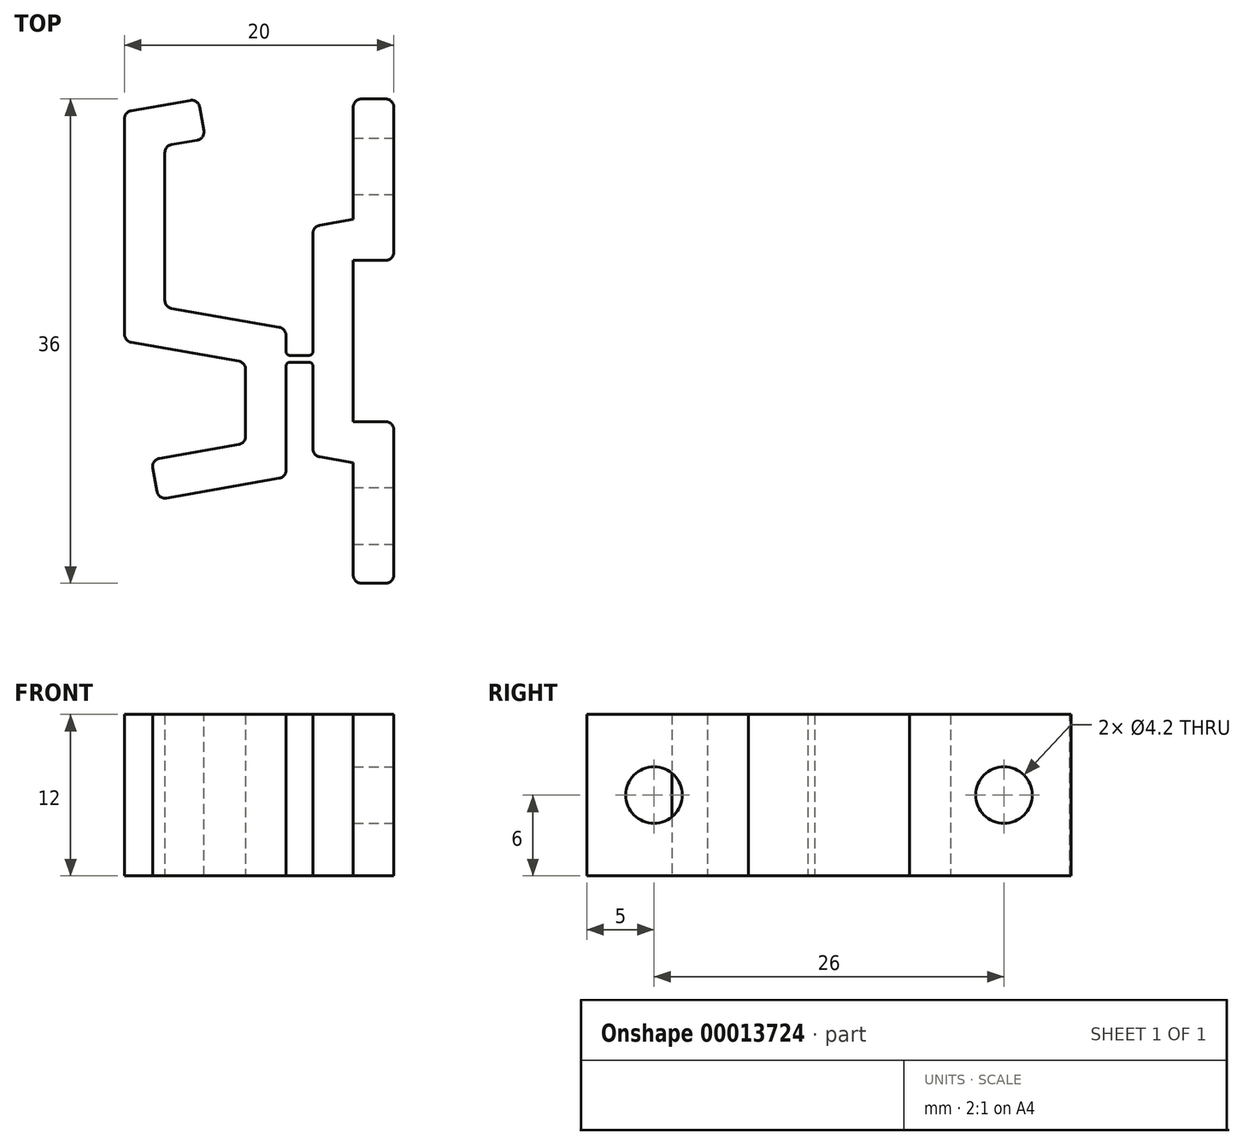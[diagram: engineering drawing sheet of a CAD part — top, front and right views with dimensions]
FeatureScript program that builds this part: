
annotation { "Feature Type Name" : "Feature", "Feature Type Description" : "" }
export const myFeature = defineFeature(function(context is Context, id is Id, definition is map)
    precondition{}
    {
        {
            var Q0;
            Q0=qCreatedBy(makeId("Top.planeOp"),FACE);
            var sketch = newSketch(context, id + "F0", { "sketchPlane" : qUnion([Q0])});
            skLineSegment(sketch, "E0", {"start": v(0, 0) * mm, "end": v(0, -12) * mm});
            skLineSegment(sketch, "E1", {"start": v(0, -12) * mm, "end": v(3, -12) * mm});
            skLineSegment(sketch, "E2", {"start": v(3, -12) * mm, "end": v(3, -24) * mm});
            skLineSegment(sketch, "E3", {"start": v(3, -24) * mm, "end": v(0, -24) * mm});
            skLineSegment(sketch, "E4", {"start": v(0, -24) * mm, "end": v(0, -15.05) * mm});
            skLineSegment(sketch, "E5", {"start": v(0, -15.05) * mm, "end": v(-3, -14.52) * mm});
            skLineSegment(sketch, "E6", {"start": v(-3, -14.52) * mm, "end": v(-3, 2.52) * mm});
            skLineSegment(sketch, "E7", {"start": v(-3, 2.52) * mm, "end": v(0, 3.05) * mm});
            skLineSegment(sketch, "E8", {"start": v(0, 3.05) * mm, "end": v(0, 12) * mm});
            skLineSegment(sketch, "E9", {"start": v(0, 12) * mm, "end": v(3, 12) * mm});
            skLineSegment(sketch, "E10", {"start": v(3, 12) * mm, "end": v(3, 0) * mm});
            skLineSegment(sketch, "E11", {"start": v(0, 0) * mm, "end": v(3, 0) * mm});
            skLineSegment(sketch, "E12", {"start": v(-5, -5.07) * mm, "end": v(-5, -16.1) * mm});
            skLineSegment(sketch, "E13", {"start": v(-5, -5.07) * mm, "end": v(-14, -3.48) * mm});
            skLineSegment(sketch, "E14", {"start": v(-5, -16.1) * mm, "end": v(-14.48, -17.78) * mm});
            skLineSegment(sketch, "E15", {"start": v(-14.48, -17.78) * mm, "end": v(-15, -14.82) * mm});
            skLineSegment(sketch, "E16", {"start": v(-15, -14.82) * mm, "end": v(-8, -13.59) * mm});
            skLineSegment(sketch, "E17", {"start": v(-8, -13.59) * mm, "end": v(-8, -7.59) * mm});
            skLineSegment(sketch, "E18", {"start": v(-8, -7.59) * mm, "end": v(-17, -6) * mm});
            skLineSegment(sketch, "E19", {"start": v(-14, -3.48) * mm, "end": v(-14, 8.52) * mm});
            skLineSegment(sketch, "E20", {"start": v(-14, 8.52) * mm, "end": v(-11, 9.05) * mm});
            skLineSegment(sketch, "E21", {"start": v(-11.52, 12) * mm, "end": v(-17, 11.03) * mm});
            skLineSegment(sketch, "E22", {"start": v(-17, 11.03) * mm, "end": v(-17, -6) * mm});
            skLineSegment(sketch, "E23", {"start": v(-11.52, 12) * mm, "end": v(-11, 9.05) * mm});
            skLineSegment(sketch, "E24", {"start": v(-3, -7.57) * mm, "end": v(-5, -7.57) * mm});
            skLineSegment(sketch, "E25", {"start": v(-3, -7.07) * mm, "end": v(-5, -7.07) * mm});
            skSolve(sketch);
        }
        {
            var Q0;
            {var subQ1=sQuery(id+"F0.wireOp",EDGE,"E13");Q0=makeQuery(id+"F0.imprint","IMPRINT",FACE,{"disambiguationData":[TD([[makeQuery(id+"F0.imprint","IMPRINT",EDGE,{"derivedFrom":subQ1}),1.0]])]});}
            var Q1;
            {var subQ1=sQuery(id+"F0.wireOp",EDGE,"E24");Q1=makeQuery(id+"F0.imprint","IMPRINT",FACE,{"disambiguationData":[TD([[makeQuery(id+"F0.imprint","IMPRINT",EDGE,{"derivedFrom":subQ1}),-1.0]])]});}
            var Q2;
            Q2=makeQuery(id+"F0.imprint","IMPRINT",FACE,{"disambiguationData":[TD([[makeQuery(id+"F0.imprint","IMPRINT",EDGE,{"derivedFrom":sQuery(id+"F0.wireOp",EDGE,"E0")}),-1.0]])]});
            extrude(context, id + "F1", {"entities" : qUnion([Q0, Q1, Q2]), "depth" : 12 * mm});
        }
        {
            var Q0;
            Q0=makeQuery(id+"F1.opExtrude","SWEPT_FACE",FACE,{"disambiguationData":[OSD([sQuery(id+"F0.wireOp",EDGE,"E2")])]});
            var sketch = newSketch(context, id + "F2", { "sketchPlane" : qUnion([Q0])});
            skLineSegment(sketch, "E26", {"start": v(-24, 6) * mm, "end": v(-19, 6) * mm, "construction": true});
            skLineSegment(sketch, "E27.0", {"start": v(12, 12) * mm, "end": v(12, 0) * mm});
            skLineSegment(sketch, "E28", {"start": v(12, 6) * mm, "end": v(7, 6) * mm, "construction": true});
            skCircle(sketch, "E29", {"center": v(-19, 6) * mm, "radius": 2.1 * mm});
            skCircle(sketch, "E30", {"center": v(7, 6) * mm, "radius": 2.1 * mm});
            skSolve(sketch);
        }
        {
            var Q0;
            Q0=makeQuery(id+"F2.imprint","IMPRINT",FACE,{"disambiguationData":[TD([[makeQuery(id+"F2.imprint","IMPRINT",EDGE,{"derivedFrom":sQuery(id+"F2.wireOp",EDGE,"E29")}),1.0]])]});
            var Q1;
            Q1=makeQuery(id+"F2.imprint","IMPRINT",FACE,{"disambiguationData":[TD([[makeQuery(id+"F2.imprint","IMPRINT",EDGE,{"derivedFrom":sQuery(id+"F2.wireOp",EDGE,"E30")}),1.0]])]});
            extrude(context, id + "F3", {"entities" : qUnion([Q0, Q1]), "operationType" : NewBodyOperationType.REMOVE, "endBound" : BoundingType.UP_TO_NEXT, "oppositeDirection" : true, "depth" : 25 * mm});
        }
        {
            var Q0;
            Q0=makeQuery(id+"F1.opExtrude","SWEPT_EDGE",EDGE,{"disambiguationData":[OSD([sQuery(id+"F0.wireOp",EDGE,"E21"),sQuery(id+"F0.wireOp",EDGE,"E23")])]});
            var Q1;
            Q1=makeQuery(id+"F1.opExtrude","SWEPT_EDGE",EDGE,{"disambiguationData":[OSD([sQuery(id+"F0.wireOp",EDGE,"E21"),sQuery(id+"F0.wireOp",EDGE,"E22")])]});
            var Q2;
            Q2=makeQuery(id+"F1.opExtrude","SWEPT_EDGE",EDGE,{"disambiguationData":[OSD([sQuery(id+"F0.wireOp",EDGE,"E18"),sQuery(id+"F0.wireOp",EDGE,"E22")])]});
            var Q3;
            Q3=makeQuery(id+"F1.opExtrude","SWEPT_EDGE",EDGE,{"disambiguationData":[OSD([sQuery(id+"F0.wireOp",EDGE,"E17"),sQuery(id+"F0.wireOp",EDGE,"E18")])]});
            var Q4;
            Q4=makeQuery(id+"F1.opExtrude","SWEPT_EDGE",EDGE,{"disambiguationData":[OSD([sQuery(id+"F0.wireOp",EDGE,"E16"),sQuery(id+"F0.wireOp",EDGE,"E17")])]});
            var Q5;
            Q5=makeQuery(id+"F1.opExtrude","SWEPT_EDGE",EDGE,{"disambiguationData":[OSD([sQuery(id+"F0.wireOp",EDGE,"E15"),sQuery(id+"F0.wireOp",EDGE,"E16")])]});
            var Q6;
            Q6=makeQuery(id+"F1.opExtrude","SWEPT_EDGE",EDGE,{"disambiguationData":[OSD([sQuery(id+"F0.wireOp",EDGE,"E14"),sQuery(id+"F0.wireOp",EDGE,"E15")])]});
            var Q7;
            Q7=makeQuery(id+"F1.opExtrude","SWEPT_EDGE",EDGE,{"disambiguationData":[OSD([sQuery(id+"F0.wireOp",EDGE,"E12"),sQuery(id+"F0.wireOp",EDGE,"E14")])]});
            var Q8;
            Q8=makeQuery(id+"F1.opExtrude","SWEPT_EDGE",EDGE,{"disambiguationData":[OSD([sQuery(id+"F0.wireOp",EDGE,"E12"),sQuery(id+"F0.wireOp",EDGE,"E13")])]});
            var Q9;
            Q9=makeQuery(id+"F1.opExtrude","SWEPT_EDGE",EDGE,{"disambiguationData":[OSD([sQuery(id+"F0.wireOp",EDGE,"E13"),sQuery(id+"F0.wireOp",EDGE,"E19")])]});
            var Q10;
            Q10=makeQuery(id+"F1.opExtrude","SWEPT_EDGE",EDGE,{"disambiguationData":[OSD([sQuery(id+"F0.wireOp",EDGE,"E19"),sQuery(id+"F0.wireOp",EDGE,"E20")])]});
            var Q11;
            Q11=makeQuery(id+"F1.opExtrude","SWEPT_EDGE",EDGE,{"disambiguationData":[OSD([sQuery(id+"F0.wireOp",EDGE,"E20"),sQuery(id+"F0.wireOp",EDGE,"E23")])]});
            var Q12;
            Q12=makeQuery(id+"F1.opExtrude","SWEPT_EDGE",EDGE,{"disambiguationData":[OSD([sQuery(id+"F0.wireOp",EDGE,"E3"),sQuery(id+"F0.wireOp",EDGE,"E4")])]});
            var Q13;
            Q13=makeQuery(id+"F1.opExtrude","SWEPT_EDGE",EDGE,{"disambiguationData":[OSD([sQuery(id+"F0.wireOp",EDGE,"E2"),sQuery(id+"F0.wireOp",EDGE,"E3")])]});
            var Q14;
            Q14=makeQuery(id+"F1.opExtrude","SWEPT_EDGE",EDGE,{"disambiguationData":[OSD([sQuery(id+"F0.wireOp",EDGE,"E1"),sQuery(id+"F0.wireOp",EDGE,"E2")])]});
            var Q15;
            Q15=makeQuery(id+"F1.opExtrude","SWEPT_EDGE",EDGE,{"disambiguationData":[OSD([sQuery(id+"F0.wireOp",EDGE,"E10"),sQuery(id+"F0.wireOp",EDGE,"E11")])]});
            var Q16;
            Q16=makeQuery(id+"F1.opExtrude","SWEPT_EDGE",EDGE,{"disambiguationData":[OSD([sQuery(id+"F0.wireOp",EDGE,"E9"),sQuery(id+"F0.wireOp",EDGE,"E10")])]});
            var Q17;
            Q17=makeQuery(id+"F1.opExtrude","SWEPT_EDGE",EDGE,{"disambiguationData":[OSD([sQuery(id+"F0.wireOp",EDGE,"E8"),sQuery(id+"F0.wireOp",EDGE,"E9")])]});
            var Q18;
            Q18=makeQuery(id+"F1.opExtrude","SWEPT_EDGE",EDGE,{"disambiguationData":[OSD([sQuery(id+"F0.wireOp",EDGE,"E6"),sQuery(id+"F0.wireOp",EDGE,"E7")])]});
            var Q19;
            Q19=makeQuery(id+"F1.opExtrude","SWEPT_EDGE",EDGE,{"disambiguationData":[OSD([sQuery(id+"F0.wireOp",EDGE,"E5"),sQuery(id+"F0.wireOp",EDGE,"E6")])]});
            fillet(context, id + "F4", {"entities" : qUnion([Q0, Q1, Q2, Q3, Q4, Q5, Q6, Q7, Q8, Q9, Q10, Q11, Q12, Q13, Q14, Q15, Q16, Q17, Q18, Q19]), "radius" : 0.6 * mm, "tangentPropagation" : true, "allowEdgeOverflow" : false});
        }
        {
            var Q0;
            Q0=makeQuery(id+"F1.opExtrude","SWEPT_EDGE",EDGE,{"disambiguationData":[OSD([sQuery(id+"F0.wireOp",EDGE,"E6"),sQuery(id+"F0.wireOp",EDGE,"E25")])]});
            var Q1;
            Q1=makeQuery(id+"F1.opExtrude","SWEPT_EDGE",EDGE,{"disambiguationData":[OSD([sQuery(id+"F0.wireOp",EDGE,"E12"),sQuery(id+"F0.wireOp",EDGE,"E25")])]});
            var Q2;
            Q2=makeQuery(id+"F1.opExtrude","SWEPT_EDGE",EDGE,{"disambiguationData":[OSD([sQuery(id+"F0.wireOp",EDGE,"E12"),sQuery(id+"F0.wireOp",EDGE,"E24")])]});
            var Q3;
            Q3=makeQuery(id+"F1.opExtrude","SWEPT_EDGE",EDGE,{"disambiguationData":[OSD([sQuery(id+"F0.wireOp",EDGE,"E6"),sQuery(id+"F0.wireOp",EDGE,"E24")])]});
            fillet(context, id + "F5", {"entities" : qUnion([Q0, Q1, Q2, Q3]), "radius" : 0.3 * mm, "tangentPropagation" : true, "allowEdgeOverflow" : false});
        }
    });
